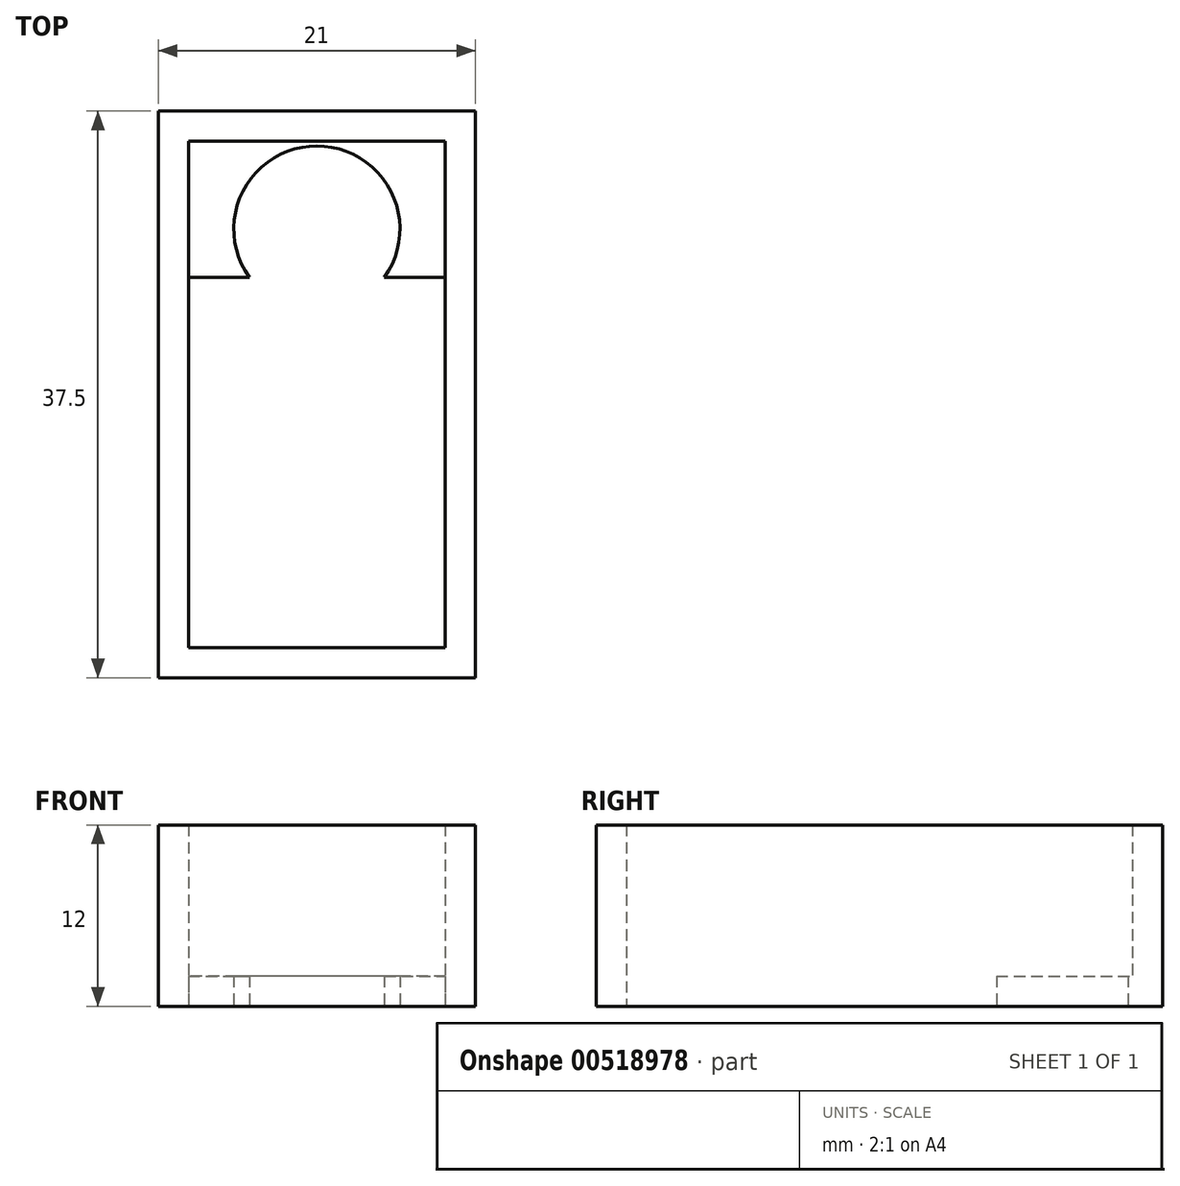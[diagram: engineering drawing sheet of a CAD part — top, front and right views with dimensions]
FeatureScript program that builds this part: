
annotation { "Feature Type Name" : "Feature", "Feature Type Description" : "" }
export const myFeature = defineFeature(function(context is Context, id is Id, definition is map)
    precondition{}
    {
        {
            var Q0;
            Q0=qCreatedBy(makeId("Top.planeOp"),FACE);
            var sketch = newSketch(context, id + "F0", { "sketchPlane" : qUnion([Q0])});
            skLineSegment(sketch, "E0.bottom", {"start": v(-9.66, 7.75) * mm, "end": v(7.34, 7.75) * mm});
            skLineSegment(sketch, "E0.top", {"start": v(-9.66, -25.75) * mm, "end": v(7.34, -25.75) * mm});
            skLineSegment(sketch, "E0.left", {"start": v(-9.66, 7.75) * mm, "end": v(-9.66, -25.75) * mm});
            skLineSegment(sketch, "E0.right", {"start": v(7.34, 7.75) * mm, "end": v(7.34, -25.75) * mm});
            skLineSegment(sketch, "E1.bottom", {"start": v(-11.66, 9.75) * mm, "end": v(9.34, 9.75) * mm});
            skLineSegment(sketch, "E1.top", {"start": v(-11.66, -27.75) * mm, "end": v(9.34, -27.75) * mm});
            skLineSegment(sketch, "E1.left", {"start": v(-11.66, 9.75) * mm, "end": v(-11.66, -27.75) * mm});
            skLineSegment(sketch, "E1.right", {"start": v(9.34, 9.75) * mm, "end": v(9.34, -27.75) * mm});
            skLineSegment(sketch, "E2", {"start": v(7.34, 0) * mm, "end": v(9.34, 0) * mm, "construction": true});
            skLineSegment(sketch, "E3", {"start": v(-9.66, 5.82) * mm, "end": v(-11.66, 5.82) * mm, "construction": true});
            skLineSegment(sketch, "E4", {"start": v(13.26, 7.75) * mm, "end": v(13.26, 9.75) * mm, "construction": true});
            skLineSegment(sketch, "E5", {"start": v(14.78, -25.75) * mm, "end": v(14.78, -27.75) * mm, "construction": true});
            skLineSegment(sketch, "E6.top", {"start": v(-9.66, -1.25) * mm, "end": v(7.34, -1.25) * mm});
            skLineSegment(sketch, "E6.left", {"start": v(-9.66, 7.75) * mm, "end": v(-9.66, -1.25) * mm});
            skLineSegment(sketch, "E6.right", {"start": v(7.34, 7.75) * mm, "end": v(7.34, -1.25) * mm});
            skLineSegment(sketch, "E7.top", {"start": v(-9.66, -16.75) * mm, "end": v(7.34, -16.75) * mm});
            skLineSegment(sketch, "E7.left", {"start": v(-9.66, -25.75) * mm, "end": v(-9.66, -16.75) * mm});
            skLineSegment(sketch, "E7.right", {"start": v(7.34, -25.75) * mm, "end": v(7.34, -16.75) * mm});
            skCircle(sketch, "E8", {"center": v(-1.16, 1.95) * mm, "radius": 5.5 * mm});
            skCircle(sketch, "E9", {"center": v(-1.16, -19.95) * mm, "radius": 5.5 * mm});
            skLineSegment(sketch, "E10", {"start": v(-1.16, 7.75) * mm, "end": v(-1.16, 1.95) * mm, "construction": true});
            skLineSegment(sketch, "E11", {"start": v(-1.16, -25.75) * mm, "end": v(-1.16, -19.95) * mm, "construction": true});
            skLineSegment(sketch, "E12.bottom", {"start": v(-5.16, 9.75) * mm, "end": v(2.84, 9.75) * mm});
            skLineSegment(sketch, "E12.top", {"start": v(-5.16, 17.75) * mm, "end": v(2.84, 17.75) * mm});
            skLineSegment(sketch, "E12.left", {"start": v(-5.16, 9.75) * mm, "end": v(-5.16, 17.75) * mm});
            skLineSegment(sketch, "E12.right", {"start": v(2.84, 9.75) * mm, "end": v(2.84, 17.75) * mm});
            skLineSegment(sketch, "E13.bottom", {"start": v(-5.16, -27.75) * mm, "end": v(2.84, -27.75) * mm});
            skLineSegment(sketch, "E13.top", {"start": v(-5.16, -35.75) * mm, "end": v(2.84, -35.75) * mm});
            skLineSegment(sketch, "E13.left", {"start": v(-5.16, -27.75) * mm, "end": v(-5.16, -35.75) * mm});
            skLineSegment(sketch, "E13.right", {"start": v(2.84, -27.75) * mm, "end": v(2.84, -35.75) * mm});
            skCircle(sketch, "E14", {"center": v(-1.16, -31.5) * mm, "radius": 1.7 * mm});
            skCircle(sketch, "E15", {"center": v(-1.16, 13.5) * mm, "radius": 1.7 * mm});
            skLineSegment(sketch, "E16", {"start": v(-1.16, -31.5) * mm, "end": v(-1.16, -27.75) * mm, "construction": true});
            skLineSegment(sketch, "E17", {"start": v(-1.16, 13.5) * mm, "end": v(-1.16, 9.75) * mm, "construction": true});
            skSolve(sketch);
        }
        {
            var Q0;
            Q0=makeQuery(id+"F0.imprint","IMPRINT",FACE,{"disambiguationData":[TD([[makeQuery(id+"F0.imprint","IMPRINT",EDGE,{"derivedFrom":sQuery(id+"F0.wireOp",EDGE,"E0.left")}),-1.0]])]});
            var Q1;
            Q1=makeQuery(id+"F0.imprint","IMPRINT",FACE,{"disambiguationData":[TD([[makeQuery(id+"F0.imprint","IMPRINT",EDGE,{"derivedFrom":sQuery(id+"F0.wireOp",EDGE,"E0.bottom")}),-1.0]])]});
            var Q2;
            Q2=makeQuery(id+"F0.imprint","IMPRINT",FACE,{"disambiguationData":[TD([[makeQuery(id+"F0.imprint","IMPRINT",EDGE,{"derivedFrom":sQuery(id+"F0.wireOp",EDGE,"E0.top")}),1.0]])]});
            var Q3;
            Q3=makeQuery(id+"F0.imprint","IMPRINT",FACE,{"disambiguationData":[TD([[makeQuery(id+"F0.imprint","IMPRINT",EDGE,{"derivedFrom":sQuery(id+"F0.wireOp",EDGE,"E12.bottom")}),1.0]])]});
            var Q4;
            Q4=makeQuery(id+"F0.imprint","IMPRINT",FACE,{"disambiguationData":[TD([[makeQuery(id+"F0.imprint","IMPRINT",EDGE,{"derivedFrom":sQuery(id+"F0.wireOp",EDGE,"E13.bottom")}),-1.0]])]});
            extrude(context, id + "F1", {"entities" : qUnion([Q0, Q1, Q2, Q3, Q4]), "depth" : 2 * mm, "offsetDistance" : 25 * mm});
        }
        {
            var Q0;
            Q0=makeQuery(id+"F0.imprint","IMPRINT",FACE,{"disambiguationData":[TD([[makeQuery(id+"F0.imprint","IMPRINT",EDGE,{"derivedFrom":sQuery(id+"F0.wireOp",EDGE,"E0.left")}),-1.0]])]});
            extrude(context, id + "F2", {"entities" : qUnion([Q0]), "operationType" : NewBodyOperationType.ADD, "depth" : 12 * mm, "offsetDistance" : 25 * mm});
        }
    });
